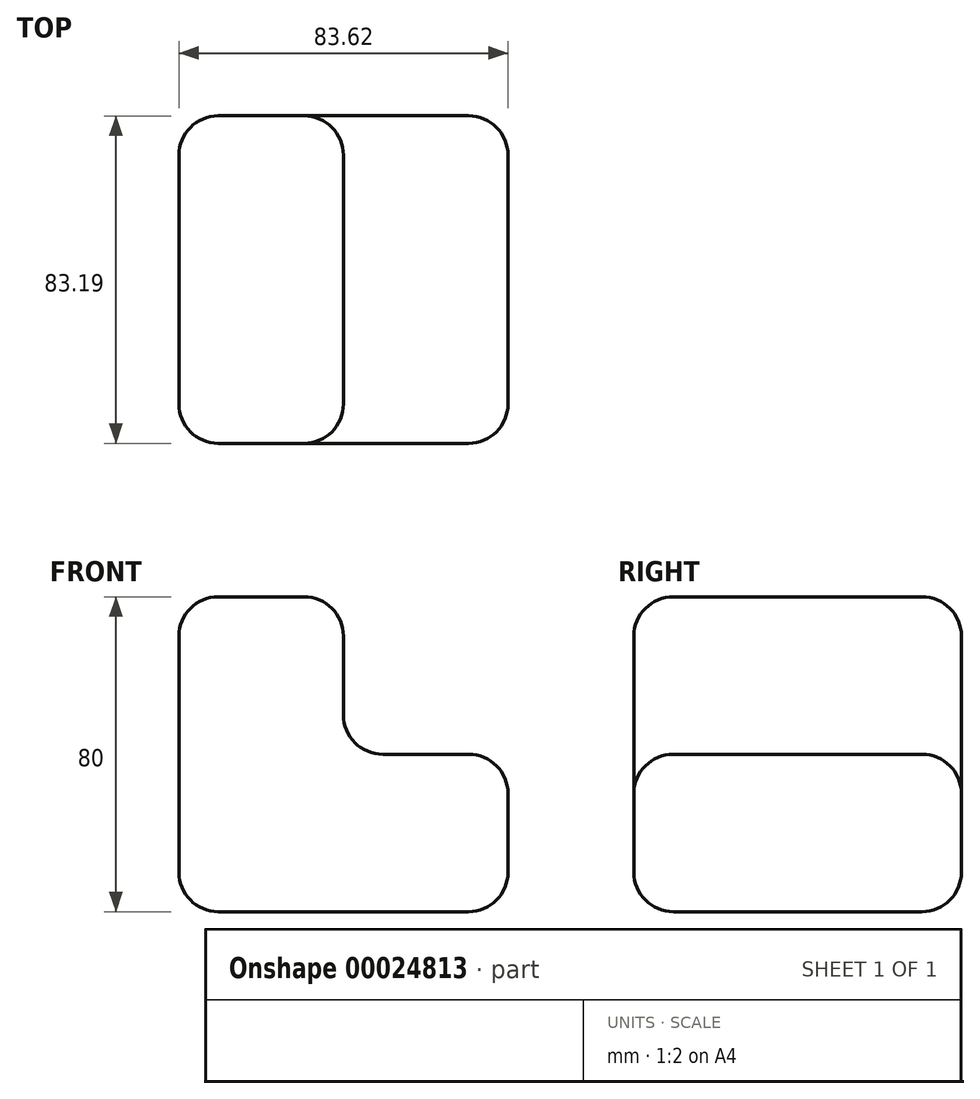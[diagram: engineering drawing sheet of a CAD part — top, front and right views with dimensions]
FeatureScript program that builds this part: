
annotation { "Feature Type Name" : "Feature", "Feature Type Description" : "" }
export const myFeature = defineFeature(function(context is Context, id is Id, definition is map)
    precondition{}
    {
        {
            var Q0;
            Q0=qCreatedBy(makeId("Top.planeOp"),FACE);
            var sketch = newSketch(context, id + "F0", { "sketchPlane" : qUnion([Q0])});
            skLineSegment(sketch, "E0.bottom", {"start": v(-59.13, -45.93) * mm, "end": v(24.5, -45.93) * mm});
            skLineSegment(sketch, "E0.top", {"start": v(-59.13, 37.26) * mm, "end": v(24.5, 37.26) * mm});
            skLineSegment(sketch, "E0.left", {"start": v(-59.13, -45.93) * mm, "end": v(-59.13, 37.26) * mm});
            skLineSegment(sketch, "E0.right", {"start": v(24.5, -45.93) * mm, "end": v(24.5, 37.26) * mm});
            skSolve(sketch);
        }
        {
            var Q0;
            Q0=makeQuery(id+"F0.imprint","IMPRINT",FACE,{"disambiguationData":[TD([[makeQuery(id+"F0.imprint","IMPRINT",EDGE,{"derivedFrom":sQuery(id+"F0.wireOp",EDGE,"E0.bottom")}),1.0]])]});
            extrude(context, id + "F1", {"entities" : qUnion([Q0]), "depth" : 40 * mm});
        }
        {
            var Q0;
            Q0=makeQuery(id+"F1.opExtrude","CAP_FACE",FACE,{"disambiguationData":[OSD([sQuery(id+"F0.wireOp",EDGE,"E0.bottom"),sQuery(id+"F0.wireOp",EDGE,"E0.top"),sQuery(id+"F0.wireOp",EDGE,"E0.left"),sQuery(id+"F0.wireOp",EDGE,"E0.right")])],"isStart":false});
            var sketch = newSketch(context, id + "F2", { "sketchPlane" : qUnion([Q0])});
            skLineSegment(sketch, "E1", {"start": v(-17.32, 37.26) * mm, "end": v(-17.32, -45.93) * mm});
            skSolve(sketch);
        }
        {
            var Q0;
            {var subQ1=sQuery(id+"F2.wireOp",EDGE,"E1");Q0=makeQuery(id+"F2.imprint","IMPRINT",FACE,{"disambiguationData":[TD([[makeQuery(id+"F2.imprint","IMPRINT",EDGE,{"derivedFrom":subQ1}),-1.0]])]});}
            extrude(context, id + "F3", {"entities" : qUnion([Q0]), "operationType" : NewBodyOperationType.ADD, "depth" : 40 * mm});
        }
        {
            var Q0;
            {var subQ0=sQuery(id+"F0.wireOp",EDGE,"E0.bottom");Q0=makeQuery(id+"F3.boolean.opBoolean","MERGE",FACE,{"derivedFrom":[makeQuery(id+"F1.opExtrude","SWEPT_FACE",FACE,{"disambiguationData":[OSD([subQ0])]}),makeQuery(id+"F3.opExtrude","SWEPT_FACE",FACE,{"disambiguationData":[OSD([subQ0])]})]});}
            var Q1;
            Q1=makeQuery(id+"F3.opExtrude","CAP_FACE",FACE,{"disambiguationData":[OSD([sQuery(id+"F0.wireOp",EDGE,"E0.bottom"),sQuery(id+"F0.wireOp",EDGE,"E0.top"),sQuery(id+"F0.wireOp",EDGE,"E0.left"),sQuery(id+"F2.wireOp",EDGE,"E1")])],"isStart":false});
            var Q2;
            Q2=makeQuery(id+"F1.opExtrude","CAP_FACE",FACE,{"disambiguationData":[OSD([sQuery(id+"F0.wireOp",EDGE,"E0.bottom"),sQuery(id+"F0.wireOp",EDGE,"E0.top"),sQuery(id+"F0.wireOp",EDGE,"E0.left"),sQuery(id+"F0.wireOp",EDGE,"E0.right")])],"isStart":false});
            var Q3;
            {var subQ0=sQuery(id+"F0.wireOp",EDGE,"E0.left");Q3=makeQuery(id+"F3.boolean.opBoolean","MERGE",FACE,{"derivedFrom":[makeQuery(id+"F1.opExtrude","SWEPT_FACE",FACE,{"disambiguationData":[OSD([subQ0])]}),makeQuery(id+"F3.opExtrude","SWEPT_FACE",FACE,{"disambiguationData":[OSD([subQ0])]})]});}
            var Q4;
            Q4=makeQuery(id+"F1.opExtrude","CAP_FACE",FACE,{"disambiguationData":[OSD([sQuery(id+"F0.wireOp",EDGE,"E0.bottom"),sQuery(id+"F0.wireOp",EDGE,"E0.top"),sQuery(id+"F0.wireOp",EDGE,"E0.left"),sQuery(id+"F0.wireOp",EDGE,"E0.right")])],"isStart":true});
            var Q5;
            {var subQ0=sQuery(id+"F0.wireOp",EDGE,"E0.top");Q5=makeQuery(id+"F3.boolean.opBoolean","MERGE",FACE,{"derivedFrom":[makeQuery(id+"F1.opExtrude","SWEPT_FACE",FACE,{"disambiguationData":[OSD([subQ0])]}),makeQuery(id+"F3.opExtrude","SWEPT_FACE",FACE,{"disambiguationData":[OSD([subQ0])]})]});}
            fillet(context, id + "F4", {"entities" : qUnion([Q0, Q1, Q2, Q3, Q4, Q5]), "radius" : 10 * mm, "tangentPropagation" : true, "allowEdgeOverflow" : false});
        }
    });
